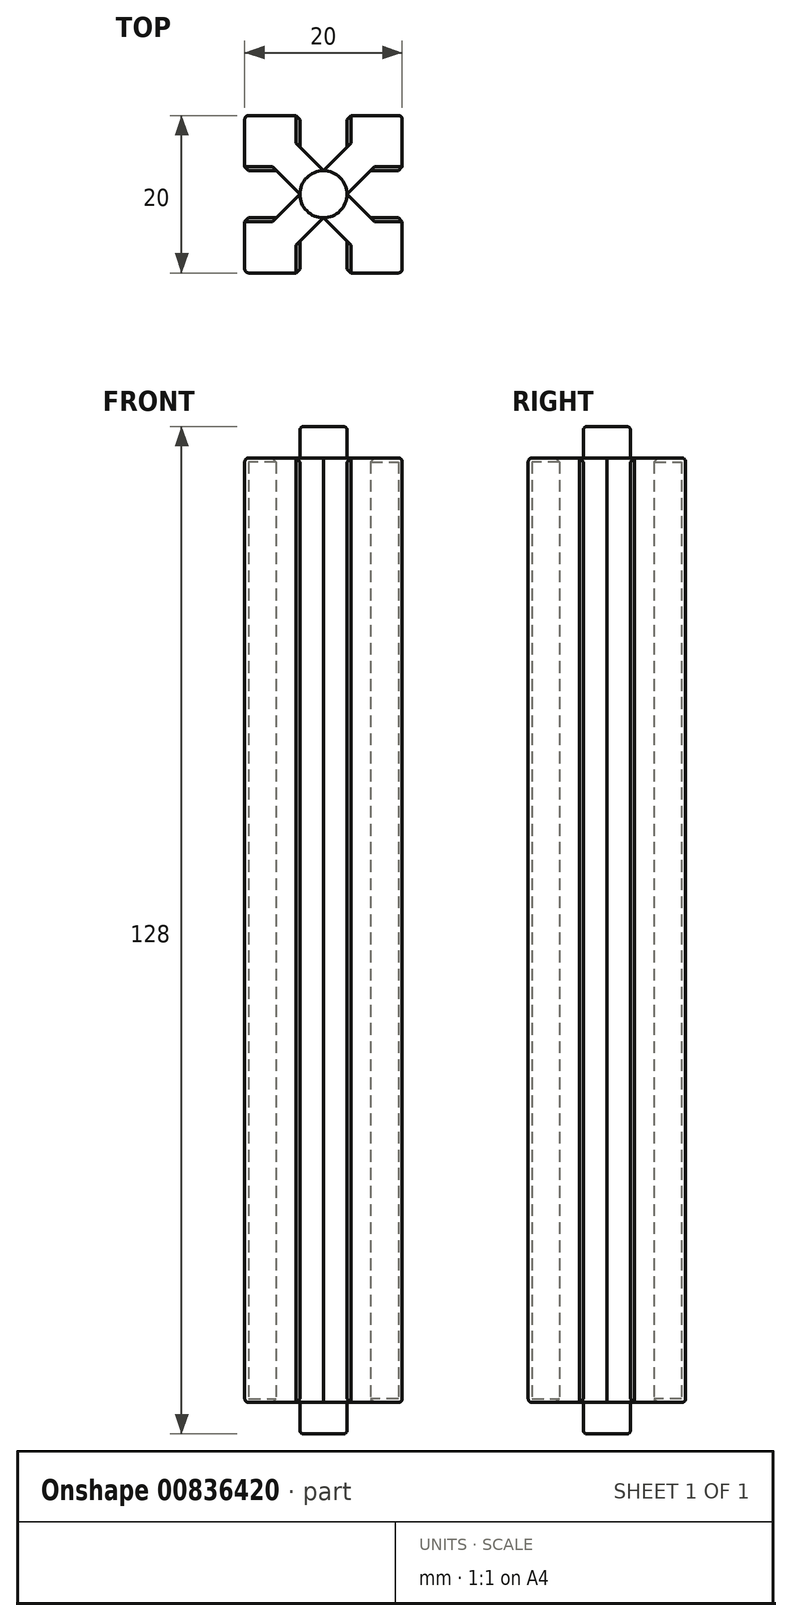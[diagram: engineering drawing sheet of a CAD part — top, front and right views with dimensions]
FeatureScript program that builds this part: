
annotation { "Feature Type Name" : "Feature", "Feature Type Description" : "" }
export const myFeature = defineFeature(function(context is Context, id is Id, definition is map)
    precondition{}
    {
        {
            var Q0;
            Q0=qCreatedBy(makeId("Top.planeOp"),FACE);
            var sketch = newSketch(context, id + "F0", { "sketchPlane" : qUnion([Q0])});
            skLineSegment(sketch, "E0.bottom", {"start": v(-10, -10) * mm, "end": v(-3, -10) * mm});
            skLineSegment(sketch, "E0.top", {"start": v(-10, 10) * mm, "end": v(-3, 10) * mm});
            skLineSegment(sketch, "E0.left", {"start": v(-10, -10) * mm, "end": v(-10, -3) * mm});
            skLineSegment(sketch, "E0.right", {"start": v(10, -10) * mm, "end": v(10, -3) * mm});
            skPoint(sketch, "E0.middle", {"position": v(0, 0) * mm});
            skLineSegment(sketch, "E1.bottom", {"start": v(-6, 3) * mm, "end": v(-10, 3) * mm});
            skLineSegment(sketch, "E1.top", {"start": v(-6, -3) * mm, "end": v(-10, -3) * mm});
            skPoint(sketch, "E1.middle", {"position": v(-10, 0) * mm});
            skPoint(sketch, "E2.orphan", {"position": v(-14, 3) * mm});
            skPoint(sketch, "E3.orphan", {"position": v(-14, -3) * mm});
            skLineSegment(sketch, "E4.left", {"start": v(-3, 6) * mm, "end": v(-3, 10) * mm});
            skLineSegment(sketch, "E4.right", {"start": v(3, 6) * mm, "end": v(3, 10) * mm});
            skPoint(sketch, "E4.middle", {"position": v(0, 10) * mm});
            skPoint(sketch, "E4.top.start.orphan", {"position": v(-3, 14) * mm});
            skPoint(sketch, "E5.orphan", {"position": v(3, 14) * mm});
            skLineSegment(sketch, "E6.left", {"start": v(-3, -6) * mm, "end": v(-3, -10) * mm});
            skLineSegment(sketch, "E6.right", {"start": v(3, -6) * mm, "end": v(3, -10) * mm});
            skPoint(sketch, "E6.middle", {"position": v(0, -10) * mm});
            skPoint(sketch, "E6.top.end.orphan", {"position": v(3, -14) * mm});
            skPoint(sketch, "E6.top.start.orphan", {"position": v(-3, -14) * mm});
            skLineSegment(sketch, "E7.bottom", {"start": v(6, 3) * mm, "end": v(10, 3) * mm});
            skLineSegment(sketch, "E7.top", {"start": v(6, -3) * mm, "end": v(10, -3) * mm});
            skPoint(sketch, "E7.middle", {"position": v(10, 0) * mm});
            skPoint(sketch, "E8.orphan", {"position": v(14, 3) * mm});
            skPoint(sketch, "E9.orphan", {"position": v(14, -3) * mm});
            skLineSegment(sketch, "E10", {"start": v(-6, 3) * mm, "end": v(-3, 0) * mm, "construction": true});
            skLineSegment(sketch, "E11", {"start": v(-3, -6) * mm, "end": v(0, -3) * mm, "construction": true});
            skLineSegment(sketch, "E12", {"start": v(-6, -3) * mm, "end": v(-3, 0) * mm, "construction": true});
            skLineSegment(sketch, "E13", {"start": v(-3, 6) * mm, "end": v(0, 3) * mm, "construction": true});
            skLineSegment(sketch, "E14", {"start": v(-6, 3) * mm, "end": v(-3, 0) * mm});
            skLineSegment(sketch, "E15", {"start": v(-3, 0) * mm, "end": v(-6, -3) * mm});
            skLineSegment(sketch, "E16", {"start": v(-3, -6) * mm, "end": v(0, -3) * mm});
            skLineSegment(sketch, "E17", {"start": v(0, -3) * mm, "end": v(3, -6) * mm});
            skLineSegment(sketch, "E18", {"start": v(6, -3) * mm, "end": v(3, 0) * mm});
            skLineSegment(sketch, "E19", {"start": v(3, 0) * mm, "end": v(6, 3) * mm});
            skLineSegment(sketch, "E20", {"start": v(3, 6) * mm, "end": v(0, 3) * mm});
            skLineSegment(sketch, "E21", {"start": v(0, 3) * mm, "end": v(-3, 6) * mm});
            skLineSegment(sketch, "E22.trimOffspring", {"start": v(0, -3) * mm, "end": v(3, -6) * mm, "construction": true});
            skLineSegment(sketch, "E23.trimOffspring", {"start": v(0, 3) * mm, "end": v(3, 6) * mm, "construction": true});
            skLineSegment(sketch, "E24.trimOffspring", {"start": v(3, 0) * mm, "end": v(6, -3) * mm, "construction": true});
            skLineSegment(sketch, "E25.trimOffspring", {"start": v(3, 0) * mm, "end": v(6, 3) * mm, "construction": true});
            skCircle(sketch, "E26", {"center": v(0, 0) * mm, "radius": 3 * mm});
            skLineSegment(sketch, "E27.trimOffspring", {"start": v(-10, 3) * mm, "end": v(-10, 10) * mm});
            skLineSegment(sketch, "E28.trimOffspring", {"start": v(3, 10) * mm, "end": v(10, 10) * mm});
            skLineSegment(sketch, "E29.trimOffspring", {"start": v(10, 3) * mm, "end": v(10, 10) * mm});
            skLineSegment(sketch, "E30.trimOffspring", {"start": v(3, -10) * mm, "end": v(10, -10) * mm});
            skSolve(sketch);
        }
        {
            var Q0;
            Q0 = qSketchRegion(id + "F0", true);
            extrude(context, id + "F1", {"entities" : qUnion([Q0]), "depth" : 120 * mm, "offsetDistance" : 25 * mm});
        }
        {
            var Q0;
            Q0=makeQuery(id+"F1.opExtrude","CAP_EDGE",EDGE,{"disambiguationData":[OSD([sQuery(id+"F0.wireOp",EDGE,"E0.top")])],"isStart":false});
            var Q1;
            Q1=makeQuery(id+"F1.opExtrude","CAP_EDGE",EDGE,{"disambiguationData":[OSD([sQuery(id+"F0.wireOp",EDGE,"E27.trimOffspring")])],"isStart":false});
            fillet(context, id + "F2", {"entities" : qUnion([Q0, Q1]), "radius" : 0.5 * mm, "tangentPropagation" : true, "allowEdgeOverflow" : false});
        }
        {
            var Q0;
            Q0=makeQuery(id+"F1.opExtrude","CAP_EDGE",EDGE,{"disambiguationData":[OSD([sQuery(id+"F0.wireOp",EDGE,"E0.left")])],"isStart":false});
            var Q1;
            Q1=makeQuery(id+"F1.opExtrude","CAP_EDGE",EDGE,{"disambiguationData":[OSD([sQuery(id+"F0.wireOp",EDGE,"E0.bottom")])],"isStart":false});
            fillet(context, id + "F3", {"entities" : qUnion([Q0, Q1]), "radius" : 0.5 * mm, "tangentPropagation" : true, "allowEdgeOverflow" : false});
        }
        {
            var Q0;
            Q0=makeQuery(id+"F1.opExtrude","CAP_EDGE",EDGE,{"disambiguationData":[OSD([sQuery(id+"F0.wireOp",EDGE,"E30.trimOffspring")])],"isStart":false});
            var Q1;
            Q1=makeQuery(id+"F1.opExtrude","CAP_EDGE",EDGE,{"disambiguationData":[OSD([sQuery(id+"F0.wireOp",EDGE,"E0.right")])],"isStart":false});
            var Q2;
            Q2=makeQuery(id+"F1.opExtrude","CAP_EDGE",EDGE,{"disambiguationData":[OSD([sQuery(id+"F0.wireOp",EDGE,"E29.trimOffspring")])],"isStart":false});
            var Q3;
            Q3=makeQuery(id+"F1.opExtrude","CAP_EDGE",EDGE,{"disambiguationData":[OSD([sQuery(id+"F0.wireOp",EDGE,"E28.trimOffspring")])],"isStart":false});
            fillet(context, id + "F4", {"entities" : qUnion([Q0, Q1, Q2, Q3]), "radius" : 0.5 * mm, "tangentPropagation" : true, "allowEdgeOverflow" : false});
        }
        {
            var Q0;
            Q0=makeQuery(id+"F1.opExtrude","SWEPT_EDGE",EDGE,{"disambiguationData":[OSD([sQuery(id+"F0.wireOp",EDGE,"E0.top"),sQuery(id+"F0.wireOp",EDGE,"E27.trimOffspring")])]});
            var Q1;
            Q1=makeQuery(id+"F1.opExtrude","SWEPT_EDGE",EDGE,{"disambiguationData":[OSD([sQuery(id+"F0.wireOp",EDGE,"E0.bottom"),sQuery(id+"F0.wireOp",EDGE,"E0.left")])]});
            var Q2;
            Q2=makeQuery(id+"F1.opExtrude","SWEPT_EDGE",EDGE,{"disambiguationData":[OSD([sQuery(id+"F0.wireOp",EDGE,"E28.trimOffspring"),sQuery(id+"F0.wireOp",EDGE,"E29.trimOffspring")])]});
            var Q3;
            Q3=makeQuery(id+"F1.opExtrude","SWEPT_EDGE",EDGE,{"disambiguationData":[OSD([sQuery(id+"F0.wireOp",EDGE,"E0.right"),sQuery(id+"F0.wireOp",EDGE,"E30.trimOffspring")])]});
            fillet(context, id + "F5", {"entities" : qUnion([Q0, Q1, Q2, Q3]), "radius" : 0.5 * mm, "tangentPropagation" : true, "allowEdgeOverflow" : false});
        }
        {
            var Q0;
            Q0=makeQuery(id+"F1.opExtrude","CAP_EDGE",EDGE,{"disambiguationData":[OSD([sQuery(id+"F0.wireOp",EDGE,"E0.right")])],"isStart":true});
            var Q1;
            Q1=makeQuery(id+"F1.opExtrude","CAP_EDGE",EDGE,{"disambiguationData":[OSD([sQuery(id+"F0.wireOp",EDGE,"E30.trimOffspring")])],"isStart":true});
            var Q2;
            Q2=makeQuery(id+"F1.opExtrude","CAP_EDGE",EDGE,{"disambiguationData":[OSD([sQuery(id+"F0.wireOp",EDGE,"E29.trimOffspring")])],"isStart":true});
            var Q3;
            Q3=makeQuery(id+"F1.opExtrude","CAP_EDGE",EDGE,{"disambiguationData":[OSD([sQuery(id+"F0.wireOp",EDGE,"E28.trimOffspring")])],"isStart":true});
            var Q4;
            Q4=makeQuery(id+"F1.opExtrude","CAP_EDGE",EDGE,{"disambiguationData":[OSD([sQuery(id+"F0.wireOp",EDGE,"E0.top")])],"isStart":true});
            var Q5;
            Q5=makeQuery(id+"F1.opExtrude","CAP_EDGE",EDGE,{"disambiguationData":[OSD([sQuery(id+"F0.wireOp",EDGE,"E27.trimOffspring")])],"isStart":true});
            var Q6;
            Q6=makeQuery(id+"F1.opExtrude","CAP_EDGE",EDGE,{"disambiguationData":[OSD([sQuery(id+"F0.wireOp",EDGE,"E0.left")])],"isStart":true});
            var Q7;
            Q7=makeQuery(id+"F1.opExtrude","CAP_EDGE",EDGE,{"disambiguationData":[OSD([sQuery(id+"F0.wireOp",EDGE,"E0.bottom")])],"isStart":true});
            fillet(context, id + "F6", {"entities" : qUnion([Q0, Q1, Q2, Q3, Q4, Q5, Q6, Q7]), "radius" : 0.5 * mm, "tangentPropagation" : true, "allowEdgeOverflow" : false});
        }
        {
            var Q0;
            Q0=makeQuery(id+"F1.opExtrude","SWEPT_EDGE",EDGE,{"disambiguationData":[OSD([sQuery(id+"F0.wireOp",EDGE,"E0.right"),sQuery(id+"F0.wireOp",EDGE,"E7.top")])]});
            var Q1;
            Q1=makeQuery(id+"F1.opExtrude","SWEPT_EDGE",EDGE,{"disambiguationData":[OSD([sQuery(id+"F0.wireOp",EDGE,"E7.bottom"),sQuery(id+"F0.wireOp",EDGE,"E29.trimOffspring")])]});
            var Q2;
            Q2=makeQuery(id+"F1.opExtrude","SWEPT_EDGE",EDGE,{"disambiguationData":[OSD([sQuery(id+"F0.wireOp",EDGE,"E0.top"),sQuery(id+"F0.wireOp",EDGE,"E4.left")])]});
            var Q3;
            Q3=makeQuery(id+"F1.opExtrude","SWEPT_EDGE",EDGE,{"disambiguationData":[OSD([sQuery(id+"F0.wireOp",EDGE,"E4.right"),sQuery(id+"F0.wireOp",EDGE,"E28.trimOffspring")])]});
            var Q4;
            Q4=makeQuery(id+"F1.opExtrude","SWEPT_EDGE",EDGE,{"disambiguationData":[OSD([sQuery(id+"F0.wireOp",EDGE,"E0.left"),sQuery(id+"F0.wireOp",EDGE,"E1.top")])]});
            var Q5;
            Q5=makeQuery(id+"F1.opExtrude","SWEPT_EDGE",EDGE,{"disambiguationData":[OSD([sQuery(id+"F0.wireOp",EDGE,"E1.bottom"),sQuery(id+"F0.wireOp",EDGE,"E27.trimOffspring")])]});
            var Q6;
            Q6=makeQuery(id+"F1.opExtrude","SWEPT_EDGE",EDGE,{"disambiguationData":[OSD([sQuery(id+"F0.wireOp",EDGE,"E6.right"),sQuery(id+"F0.wireOp",EDGE,"E30.trimOffspring")])]});
            var Q7;
            Q7=makeQuery(id+"F1.opExtrude","SWEPT_EDGE",EDGE,{"disambiguationData":[OSD([sQuery(id+"F0.wireOp",EDGE,"E0.bottom"),sQuery(id+"F0.wireOp",EDGE,"E6.left")])]});
            chamfer(context, id + "F7", {"entities" : qUnion([Q0, Q1, Q2, Q3, Q4, Q5, Q6, Q7]), "width" : 0.5 * mm, "tangentPropagation" : true});
        }
        {
            var Q0;
            Q0=makeQuery(id+"F1.opExtrude","CAP_FACE",FACE,{"disambiguationData":[OSD([sQuery(id+"F0.wireOp",EDGE,"E0.bottom"),sQuery(id+"F0.wireOp",EDGE,"E0.top"),sQuery(id+"F0.wireOp",EDGE,"E0.left"),sQuery(id+"F0.wireOp",EDGE,"E0.right"),sQuery(id+"F0.wireOp",EDGE,"E1.bottom"),sQuery(id+"F0.wireOp",EDGE,"E1.top"),sQuery(id+"F0.wireOp",EDGE,"E4.left"),sQuery(id+"F0.wireOp",EDGE,"E4.right"),sQuery(id+"F0.wireOp",EDGE,"E6.left"),sQuery(id+"F0.wireOp",EDGE,"E6.right"),sQuery(id+"F0.wireOp",EDGE,"E7.bottom"),sQuery(id+"F0.wireOp",EDGE,"E7.top"),sQuery(id+"F0.wireOp",EDGE,"E14"),sQuery(id+"F0.wireOp",EDGE,"E16"),sQuery(id+"F0.wireOp",EDGE,"E17"),sQuery(id+"F0.wireOp",EDGE,"E18"),sQuery(id+"F0.wireOp",EDGE,"E19"),sQuery(id+"F0.wireOp",EDGE,"E20"),sQuery(id+"F0.wireOp",EDGE,"E21"),sQuery(id+"F0.wireOp",EDGE,"E27.trimOffspring"),sQuery(id+"F0.wireOp",EDGE,"E28.trimOffspring"),sQuery(id+"F0.wireOp",EDGE,"E29.trimOffspring"),sQuery(id+"F0.wireOp",EDGE,"E30.trimOffspring"),sQuery(id+"F0.wireOp",EDGE,"E15")])],"isStart":false});
            var sketch = newSketch(context, id + "F8", { "sketchPlane" : qUnion([Q0])});
            skCircle(sketch, "E31", {"center": v(0, 0) * mm, "radius": 3 * mm});
            skSolve(sketch);
        }
        {
            var Q0;
            {var subQ0=sQuery(id+"F8.wireOp",EDGE,"E31");var subQ1=makeQuery(id+"F8.imprint","INTERSECT",VERTEX,{"derivedFrom":[makeQuery(id+"F1.opExtrude","CAP_EDGE",EDGE,{"disambiguationData":[OSD([sQuery(id+"F0.wireOp",EDGE,"E18")])],"isStart":false}),makeQuery(id+"F1.opExtrude","CAP_EDGE",EDGE,{"disambiguationData":[OSD([sQuery(id+"F0.wireOp",EDGE,"E19")])],"isStart":false}),subQ0]});Q0=makeQuery(id+"F8.imprint","IMPRINT",FACE,{"disambiguationData":[TD([[makeQuery(id+"F8.imprint","IMPRINT",EDGE,{"disambiguationData":[TD([[subQ1,-1.0]])],"derivedFrom":subQ0}),1.0]])]});}
            extrude(context, id + "F9", {"entities" : qUnion([Q0]), "operationType" : NewBodyOperationType.ADD, "depth" : 4 * mm, "offsetDistance" : 25 * mm});
        }
        {
            var Q0;
            Q0=makeQuery(id+"F9.opExtrude","CAP_EDGE",EDGE,{"disambiguationData":[OSD([sQuery(id+"F8.wireOp",EDGE,"E31")])],"isStart":false});
            fillet(context, id + "F10", {"entities" : qUnion([Q0]), "radius" : 0.5 * mm, "tangentPropagation" : true, "allowEdgeOverflow" : false});
        }
        {
            var Q0;
            Q0=makeQuery(id+"F1.opExtrude","CAP_FACE",FACE,{"disambiguationData":[OSD([sQuery(id+"F0.wireOp",EDGE,"E0.bottom"),sQuery(id+"F0.wireOp",EDGE,"E0.top"),sQuery(id+"F0.wireOp",EDGE,"E0.left"),sQuery(id+"F0.wireOp",EDGE,"E0.right"),sQuery(id+"F0.wireOp",EDGE,"E1.bottom"),sQuery(id+"F0.wireOp",EDGE,"E1.top"),sQuery(id+"F0.wireOp",EDGE,"E4.left"),sQuery(id+"F0.wireOp",EDGE,"E4.right"),sQuery(id+"F0.wireOp",EDGE,"E6.left"),sQuery(id+"F0.wireOp",EDGE,"E6.right"),sQuery(id+"F0.wireOp",EDGE,"E7.bottom"),sQuery(id+"F0.wireOp",EDGE,"E7.top"),sQuery(id+"F0.wireOp",EDGE,"E14"),sQuery(id+"F0.wireOp",EDGE,"E16"),sQuery(id+"F0.wireOp",EDGE,"E17"),sQuery(id+"F0.wireOp",EDGE,"E18"),sQuery(id+"F0.wireOp",EDGE,"E19"),sQuery(id+"F0.wireOp",EDGE,"E20"),sQuery(id+"F0.wireOp",EDGE,"E21"),sQuery(id+"F0.wireOp",EDGE,"E27.trimOffspring"),sQuery(id+"F0.wireOp",EDGE,"E28.trimOffspring"),sQuery(id+"F0.wireOp",EDGE,"E29.trimOffspring"),sQuery(id+"F0.wireOp",EDGE,"E30.trimOffspring"),sQuery(id+"F0.wireOp",EDGE,"E15")])],"isStart":true});
            var sketch = newSketch(context, id + "F11", { "sketchPlane" : qUnion([Q0])});
            skCircle(sketch, "E32", {"center": v(0, 0) * mm, "radius": 3 * mm});
            skSolve(sketch);
        }
        {
            var Q0;
            {var subQ0=sQuery(id+"F11.wireOp",EDGE,"E32");var subQ1=makeQuery(id+"F11.imprint","INTERSECT",VERTEX,{"derivedFrom":[makeQuery(id+"F1.opExtrude","CAP_EDGE",EDGE,{"disambiguationData":[OSD([sQuery(id+"F0.wireOp",EDGE,"E16")])],"isStart":true}),makeQuery(id+"F1.opExtrude","CAP_EDGE",EDGE,{"disambiguationData":[OSD([sQuery(id+"F0.wireOp",EDGE,"E17")])],"isStart":true}),subQ0]});Q0=makeQuery(id+"F11.imprint","IMPRINT",FACE,{"disambiguationData":[TD([[makeQuery(id+"F11.imprint","IMPRINT",EDGE,{"disambiguationData":[TD([[subQ1,1.0]])],"derivedFrom":subQ0}),1.0]])]});}
            extrude(context, id + "F12", {"entities" : qUnion([Q0]), "operationType" : NewBodyOperationType.ADD, "depth" : 4 * mm, "offsetDistance" : 25 * mm});
        }
        {
            var Q0;
            Q0=makeQuery(id+"F12.opExtrude","CAP_EDGE",EDGE,{"disambiguationData":[OSD([sQuery(id+"F11.wireOp",EDGE,"E32")])],"isStart":false});
            fillet(context, id + "F13", {"entities" : qUnion([Q0]), "radius" : 0.5 * mm, "tangentPropagation" : true, "allowEdgeOverflow" : false});
        }
    });
